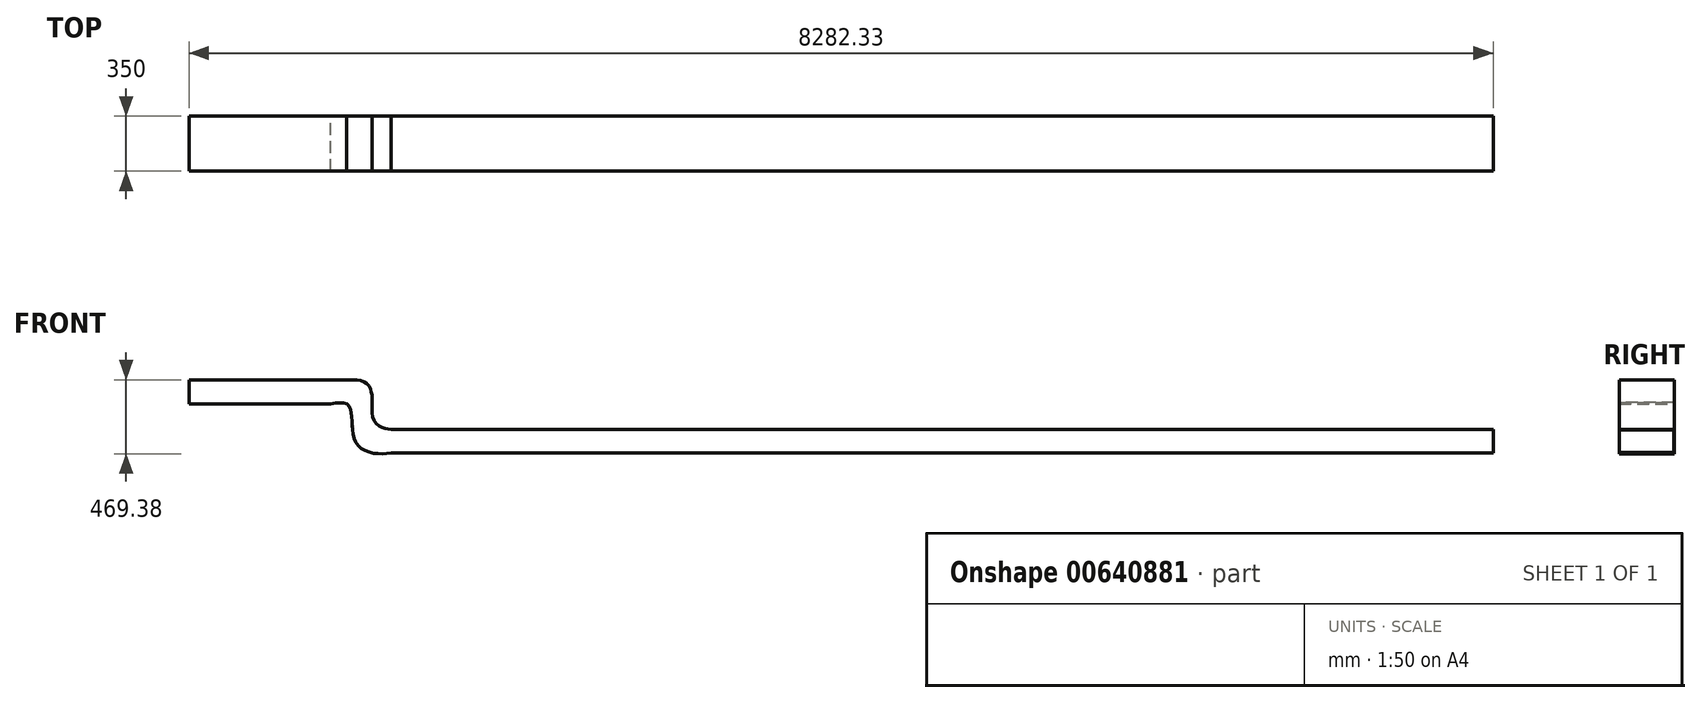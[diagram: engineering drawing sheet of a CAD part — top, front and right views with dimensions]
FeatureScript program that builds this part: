
annotation { "Feature Type Name" : "Feature", "Feature Type Description" : "" }
export const myFeature = defineFeature(function(context is Context, id is Id, definition is map)
    precondition{}
    {
        {
            var Q0;
            Q0=qCreatedBy(makeId("Front.planeOp"),FACE);
            var sketch = newSketch(context, id + "F0", { "sketchPlane" : qUnion([Q0])});
            skLineSegment(sketch, "E0", {"start": v(-2676.56, 280.9) * mm, "end": v(-1676.56, 280.9) * mm});
            skLineSegment(sketch, "E1", {"start": v(-1394.23, -31.49) * mm, "end": v(5605.77, -31.49) * mm});
            skLineSegment(sketch, "E2", {"start": v(-2676.56, 280.9) * mm, "end": v(-2676.56, 130.9) * mm});
            skLineSegment(sketch, "E3", {"start": v(-2676.56, 130.9) * mm, "end": v(-1778.14, 130.9) * mm});
            skLineSegment(sketch, "E4", {"start": v(-1394.23, -181.49) * mm, "end": v(5605.77, -181.49) * mm});
            skLineSegment(sketch, "E5", {"start": v(5605.77, -181.49) * mm, "end": v(5605.77, -31.49) * mm});
            skFitSpline(sketch, "E6", {"points": [v(-1676.56, 280.9) * mm, v(-1599.82, 280.9) * mm, v(-1539, 251.47) * mm, v(-1516.89, 190.65) * mm, v(-1514.12, 129.84) * mm, v(-1505.83, 30.32) * mm, v(-1447.78, -19.44) * mm, v(-1394.23, -31.49) * mm], "startDerivative": vector(520.8, 40.17) * mm, "endDerivative": vector(414.31, -55.13) * mm});
            skFitSpline(sketch, "E7", {"points": [v(-1778.14, 130.9) * mm, v(-1676.56, 130.9) * mm, v(-1646.81, 74.55) * mm, v(-1638.52, -31.49) * mm, v(-1608.11, -130.01) * mm, v(-1505.83, -182.54) * mm, v(-1394.23, -181.49) * mm], "startDerivative": vector(701.96, 111.3) * mm, "endDerivative": vector(622.68, 65.86) * mm});
            skSolve(sketch);
        }
        {
            var Q0;
            Q0=makeQuery(id+"F0.imprint","IMPRINT",FACE,{"disambiguationData":[TD([[makeQuery(id+"F0.imprint","IMPRINT",EDGE,{"derivedFrom":sQuery(id+"F0.wireOp",EDGE,"E0")}),-1.0]])]});
            extrude(context, id + "F1", {"entities" : qUnion([Q0]), "depth" : 350 * mm, "offsetDistance" : 25.4 * mm});
        }
        {
            var Q0;
            Q0=makeQuery(id+"F1.opExtrude","SWEPT_FACE",FACE,{"disambiguationData":[OSD([sQuery(id+"F0.wireOp",EDGE,"E2")])]});
            var Q1;
            Q1=makeQuery(id+"F1.opExtrude","SWEPT_FACE",FACE,{"disambiguationData":[OSD([sQuery(id+"F0.wireOp",EDGE,"E5")])]});
            shell(context, id + "F2", {"entities" : qUnion([Q0, Q1]), "thickness" : 2.54 * mm});
        }
    });
